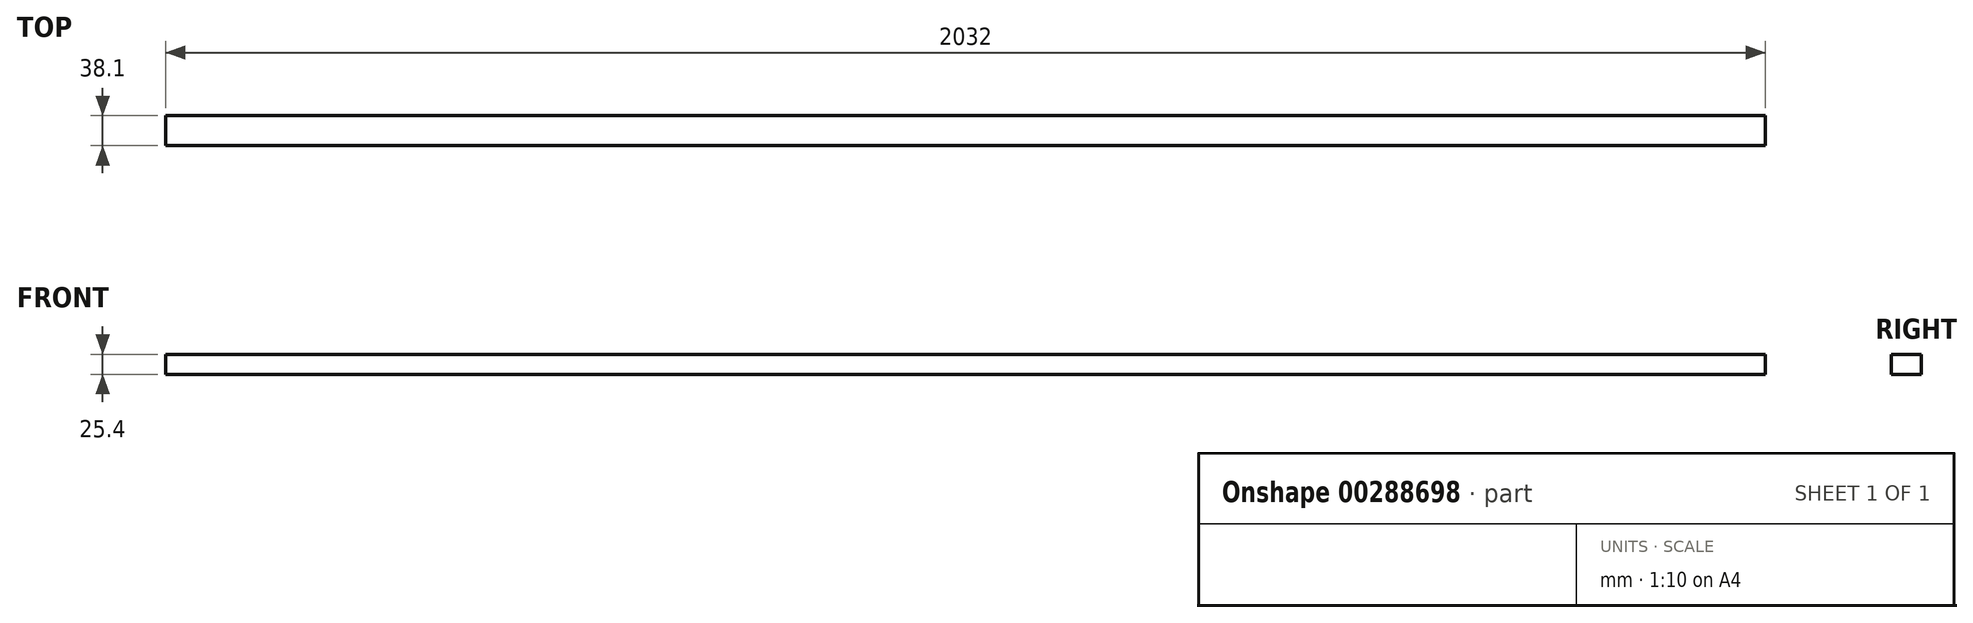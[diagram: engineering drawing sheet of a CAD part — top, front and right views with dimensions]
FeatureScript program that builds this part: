
annotation { "Feature Type Name" : "Feature", "Feature Type Description" : "" }
export const myFeature = defineFeature(function(context is Context, id is Id, definition is map)
    precondition{}
    {
        {
            var Q0;
            Q0=qCreatedBy(makeId("Front.planeOp"),FACE);
            var sketch = newSketch(context, id + "F0", { "sketchPlane" : qUnion([Q0])});
            skLineSegment(sketch, "E0.bottom", {"start": v(1016, 12.7) * mm, "end": v(-1016, 12.7) * mm});
            skLineSegment(sketch, "E0.top", {"start": v(1016, -12.7) * mm, "end": v(-1016, -12.7) * mm});
            skLineSegment(sketch, "E0.left", {"start": v(1016, 12.7) * mm, "end": v(1016, -12.7) * mm});
            skLineSegment(sketch, "E0.right", {"start": v(-1016, 12.7) * mm, "end": v(-1016, -12.7) * mm});
            skPoint(sketch, "E0.middle", {"position": v(0, 0) * mm});
            skSolve(sketch);
        }
        {
            var Q0;
            Q0=qSketchRegion(id+"F0",true);
            extrude(context, id + "F1", {"entities" : qUnion([Q0]), "endBound" : BoundingType.SYMMETRIC, "depth" : 38.1 * mm});
        }
    });
